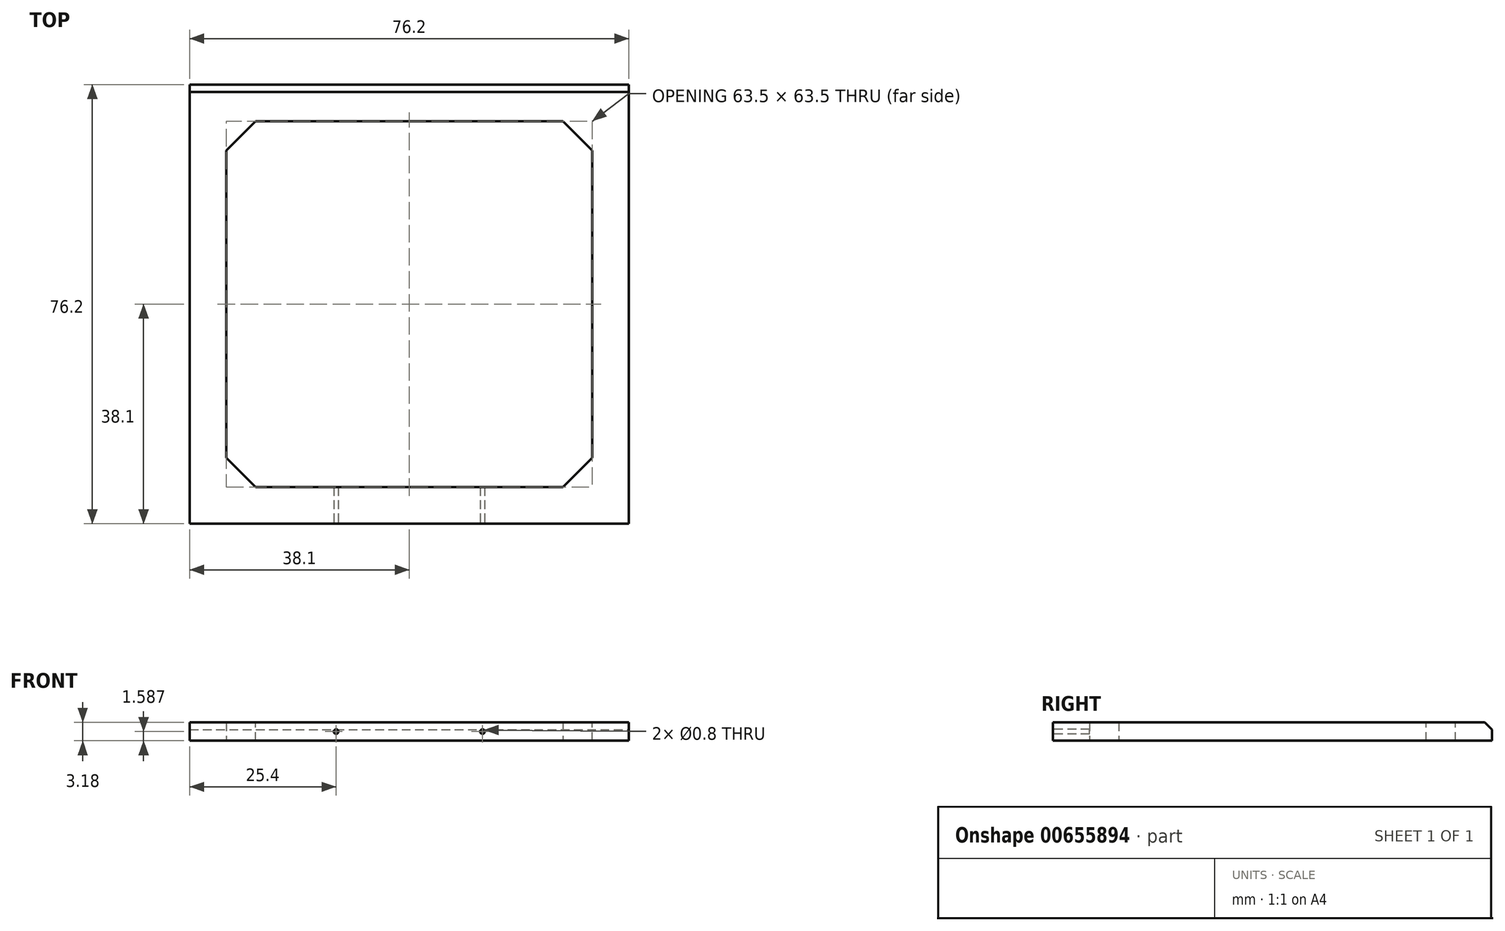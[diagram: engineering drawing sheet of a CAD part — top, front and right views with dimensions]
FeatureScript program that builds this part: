
annotation { "Feature Type Name" : "Feature", "Feature Type Description" : "" }
export const myFeature = defineFeature(function(context is Context, id is Id, definition is map)
    precondition{}
    {
        {
            var Q0;
            Q0=qCreatedBy(makeId("Top.planeOp"),FACE);
            var sketch = newSketch(context, id + "F0", { "sketchPlane" : qUnion([Q0])});
            skLineSegment(sketch, "E0.bottom", {"start": v(-38.1, -38.1) * mm, "end": v(38.1, -38.1) * mm});
            skLineSegment(sketch, "E0.top", {"start": v(-38.1, 38.1) * mm, "end": v(38.1, 38.1) * mm});
            skLineSegment(sketch, "E0.left", {"start": v(-38.1, -38.1) * mm, "end": v(-38.1, 38.1) * mm});
            skLineSegment(sketch, "E0.right", {"start": v(38.1, -38.1) * mm, "end": v(38.1, 38.1) * mm});
            skPoint(sketch, "E0.middle", {"position": v(0, 0) * mm});
            skLineSegment(sketch, "E1.bottom", {"start": v(-31.75, -31.75) * mm, "end": v(31.75, -31.75) * mm});
            skLineSegment(sketch, "E1.top", {"start": v(-31.75, 31.75) * mm, "end": v(31.75, 31.75) * mm});
            skLineSegment(sketch, "E1.left", {"start": v(-31.75, -31.75) * mm, "end": v(-31.75, 31.75) * mm});
            skLineSegment(sketch, "E1.right", {"start": v(31.75, -31.75) * mm, "end": v(31.75, 31.75) * mm});
            skSolve(sketch);
        }
        {
            var Q0;
            Q0=makeQuery(id+"F0.imprint","IMPRINT",FACE,{"disambiguationData":[TD([[makeQuery(id+"F0.imprint","IMPRINT",EDGE,{"derivedFrom":sQuery(id+"F0.wireOp",EDGE,"E0.bottom")}),1.0]])]});
            extrude(context, id + "F1", {"entities" : qUnion([Q0]), "depth" : 3.17 * mm, "offsetDistance" : 25.4 * mm});
        }
        {
            var Q0;
            Q0=makeQuery(id+"F1.opExtrude","SWEPT_EDGE",EDGE,{"disambiguationData":[OSD([sQuery(id+"F0.wireOp",EDGE,"E1.top"),sQuery(id+"F0.wireOp",EDGE,"E1.left")])]});
            chamfer(context, id + "F2", {"entities" : qUnion([Q0]), "width" : 5.08 * mm, "tangentPropagation" : true});
        }
        {
            var Q0;
            Q0=makeQuery(id+"F1.opExtrude","SWEPT_EDGE",EDGE,{"disambiguationData":[OSD([sQuery(id+"F0.wireOp",EDGE,"E1.top"),sQuery(id+"F0.wireOp",EDGE,"E1.right")])]});
            chamfer(context, id + "F3", {"entities" : qUnion([Q0]), "width" : 5.08 * mm, "tangentPropagation" : true});
        }
        {
            var Q0;
            Q0=makeQuery(id+"F1.opExtrude","SWEPT_EDGE",EDGE,{"disambiguationData":[OSD([sQuery(id+"F0.wireOp",EDGE,"E1.bottom"),sQuery(id+"F0.wireOp",EDGE,"E1.left")])]});
            chamfer(context, id + "F4", {"entities" : qUnion([Q0]), "width" : 5.08 * mm, "tangentPropagation" : true});
        }
        {
            var Q0;
            Q0=makeQuery(id+"F1.opExtrude","SWEPT_EDGE",EDGE,{"disambiguationData":[OSD([sQuery(id+"F0.wireOp",EDGE,"E1.bottom"),sQuery(id+"F0.wireOp",EDGE,"E1.right")])]});
            chamfer(context, id + "F5", {"entities" : qUnion([Q0]), "width" : 5.08 * mm, "tangentPropagation" : true});
        }
        {
            var Q0;
            Q0=makeQuery(id+"F1.opExtrude","CAP_EDGE",EDGE,{"disambiguationData":[OSD([sQuery(id+"F0.wireOp",EDGE,"E0.top")])],"isStart":false});
            chamfer(context, id + "F6", {"entities" : qUnion([Q0]), "width" : 1.27 * mm, "tangentPropagation" : true});
        }
        {
            var Q0;
            Q0=makeQuery(id+"F1.opExtrude","SWEPT_FACE",FACE,{"disambiguationData":[OSD([sQuery(id+"F0.wireOp",EDGE,"E0.bottom")])]});
            var sketch = newSketch(context, id + "F7", { "sketchPlane" : qUnion([Q0])});
            skCircle(sketch, "E2", {"center": v(-12.7, 1.59) * mm, "radius": 0.4 * mm});
            skCircle(sketch, "E3", {"center": v(12.7, 1.59) * mm, "radius": 0.4 * mm});
            skSolve(sketch);
        }
        {
            var Q0;
            Q0=makeQuery(id+"F7.imprint","IMPRINT",FACE,{"disambiguationData":[TD([[makeQuery(id+"F7.imprint","IMPRINT",EDGE,{"derivedFrom":sQuery(id+"F7.wireOp",EDGE,"E2")}),1.0]])]});
            var Q1;
            Q1=makeQuery(id+"F7.imprint","IMPRINT",FACE,{"disambiguationData":[TD([[makeQuery(id+"F7.imprint","IMPRINT",EDGE,{"derivedFrom":sQuery(id+"F7.wireOp",EDGE,"E3")}),1.0]])]});
            var Q2;
            Q2=sQuery(id+"F7.wireOp",EDGE,"E2");
            extrude(context, id + "F8", {"entities" : qUnion([Q0, Q1]), "operationType" : NewBodyOperationType.REMOVE, "surfaceEntities" : qUnion([Q2]), "oppositeDirection" : true, "depth" : 6.35 * mm, "offsetDistance" : 25.4 * mm});
        }
    });
